# Revit family: QF_ADVENTYS_ADV1742-C_D2RIC_3000
name_source: partatom
category: Attrezzature speciali
units: mm (PartAtom-declared; Revit-internal decimal feet)

## family parameters
Condiviso = No
Host = Superficie
Punto di calcolo locali = No
Quota connettore circolare = Usa diametro
Taglio con vuoti quando caricato = No
Tipo di parte = Normale

## types (1)
- ADV1742-C
    Cycle = 50 Hz
    Depth = 580 mm  [stored 1.90289 ft]
    Depth Actual = 440 mm  [stored 1.44357 ft]
    Depth_Cooking = 405 mm  [stored 1.32874 ft]
    Depth_Cutout = 550 mm
    Depth_Generator = 515.6 mm  [stored 1.6916 ft]
    EI_X = 77.6 mm  [stored 0.254593 ft]
    EI_Y = 215.8 mm  [stored 0.708005 ft]
    Height = 186 mm  [stored 0.610236 ft]
    Height Actual = 186 mm  [stored 0.610236 ft]
    Height_Generator = 84.8 mm  [stored 0.278215 ft]
    Item Number = ADV1742-C
    Length Actual = 580 mm  [stored 1.90289 ft]
    Modello = D2RIC 3000
    Phase = 1
    Produttore = ADVENTYS
    Prospetto di default = 1219.2 mm  [stored 4 ft]
    URL = https://adventys.com
    Volts = 220 V
    Watts = 3000 W
    Weight = 9.8
    Width = 440 mm  [stored 1.44357 ft]
    Width_Cooking = 342 mm  [stored 1.12205 ft]
    Width_Cutout = 410 mm  [stored 1.34514 ft]
    Width_Generator = 378 mm  [stored 1.24016 ft]

note: [stored X ft] marks values corroborated as IEEE doubles in the binary element streams (Revit-internal decimal feet)
